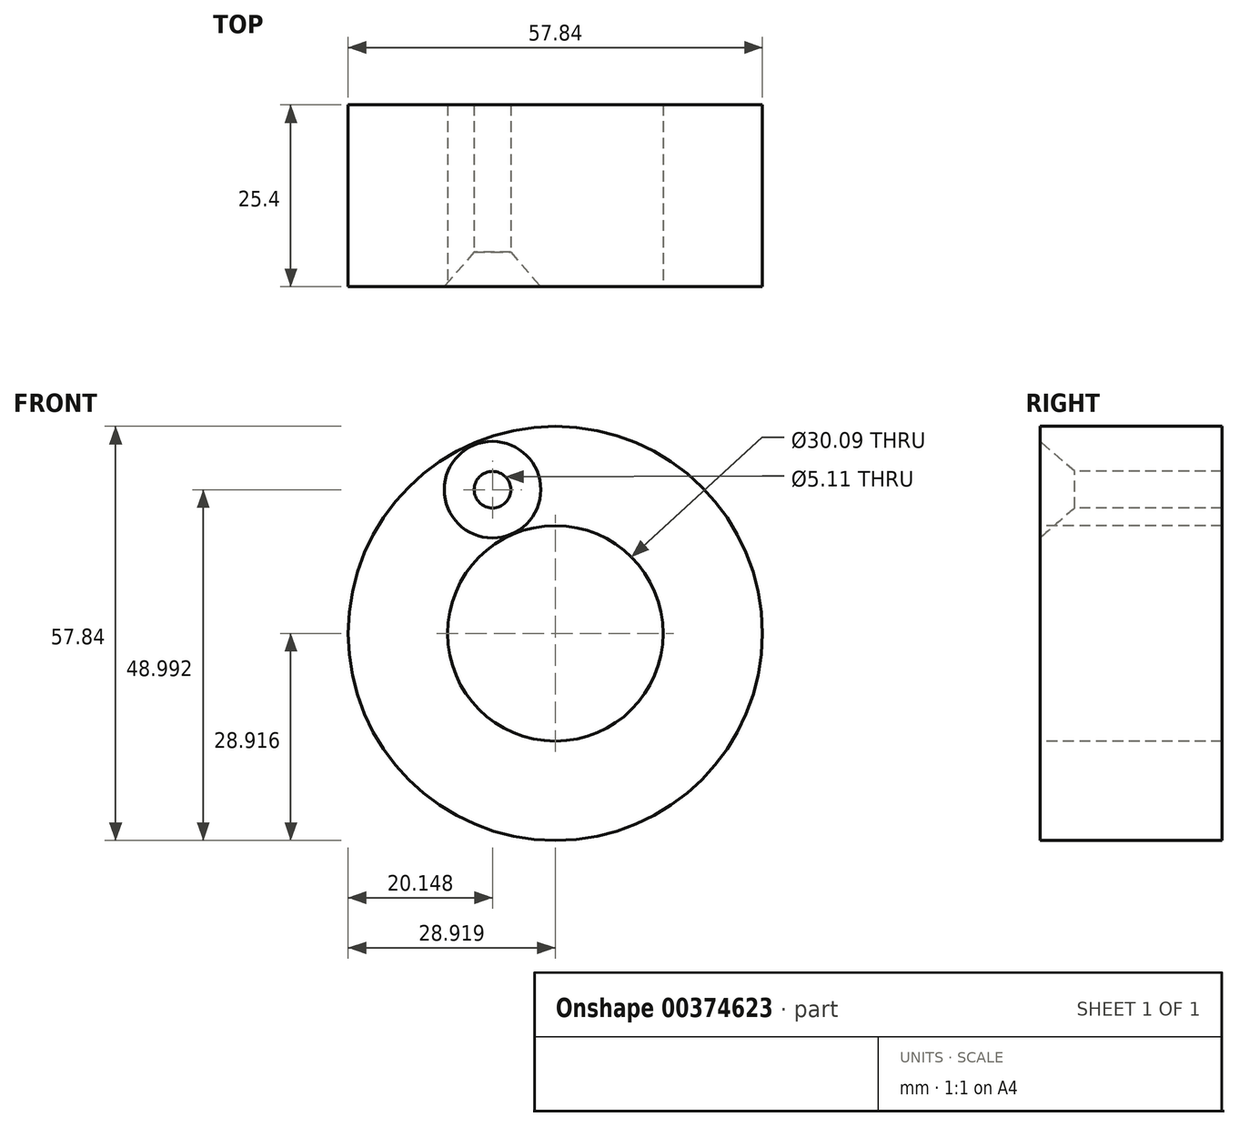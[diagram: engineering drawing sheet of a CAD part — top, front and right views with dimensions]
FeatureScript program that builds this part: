
annotation { "Feature Type Name" : "Feature", "Feature Type Description" : "" }
export const myFeature = defineFeature(function(context is Context, id is Id, definition is map)
    precondition{}
    {
        {
            var Q0;
            Q0=qCreatedBy(makeId("Front.planeOp"),FACE);
            var sketch = newSketch(context, id + "F0", { "sketchPlane" : qUnion([Q0])});
            skCircle(sketch, "E0", {"center": v(24.16, 38.02) * mm, "radius": 28.92 * mm});
            skSolve(sketch);
        }
        {
            var Q0;
            Q0=makeQuery(id+"F0.imprint","IMPRINT",FACE,{"disambiguationData":[TD([[makeQuery(id+"F0.imprint","IMPRINT",EDGE,{"derivedFrom":sQuery(id+"F0.wireOp",EDGE,"E0")}),1.0]])]});
            extrude(context, id + "F1", {"entities" : qUnion([Q0]), "depth" : 25.4 * mm});
        }
        {
            var Q0;
            Q0=makeQuery(id+"F1.opExtrude","CAP_FACE",FACE,{"disambiguationData":[OSD([sQuery(id+"F0.wireOp",EDGE,"E0")])],"isStart":false});
            var sketch = newSketch(context, id + "F2", { "sketchPlane" : qUnion([Q0])});
            skCircle(sketch, "E1", {"center": v(24.16, 38.02) * mm, "radius": 15.04 * mm});
            skSolve(sketch);
        }
        {
            var Q0;
            Q0=makeQuery(id+"F2.imprint","IMPRINT",FACE,{"disambiguationData":[TD([[makeQuery(id+"F2.imprint","IMPRINT",EDGE,{"derivedFrom":sQuery(id+"F2.wireOp",EDGE,"E1")}),1.0]])]});
            extrude(context, id + "F3", {"entities" : qUnion([Q0]), "operationType" : NewBodyOperationType.REMOVE, "endBound" : BoundingType.THROUGH_ALL, "oppositeDirection" : true, "depth" : 25.4 * mm});
        }
        {
            var Q0;
            Q0=makeQuery(id+"F1.opExtrude","CAP_FACE",FACE,{"disambiguationData":[OSD([sQuery(id+"F0.wireOp",EDGE,"E0")])],"isStart":false});
            var sketch = newSketch(context, id + "F4", { "sketchPlane" : qUnion([Q0])});
            skPoint(sketch, "E2", {"position": v(15.39, 58.1) * mm});
            skSolve(sketch);
        }
        {
            var Q0;
            Q0=sQuery(id+"F4.wireOp",VERTEX,"E2");
            var Q1;
            Q1=makeQuery(id+"F1.opExtrude","SWEPT_BODY",BODY,{"disambiguationData":[OSD([sQuery(id+"F0.wireOp",EDGE,"E0")])]});
            hole(context, id + "F5", {"style" : HoleStyle.C_SINK, "endStyle" : HoleEndStyle.THROUGH, "standardTappedOrClearance" : lookupTablePath({ "standard" : "ANSI", "engagement" : "75%", "pitch" : "20 tpi", "size" : "1/4", "type" : "Tapped" }), "standardBlindInLast" : lookupTablePath({ "standard" : "ANSI", "engagement" : "75%", "pitch" : "20 tpi", "size" : "1/4", "type" : "Tapped" }), "holeDiameter" : 5.1 * mm, "cSinkDiameter" : 13.5 * mm, "cSinkAngle" : 82 * degree, "showTappedDepth" : true, "isTappedThrough" : true, "tappedDepth" : 12.7 * mm, "tapClearance" : 3, "locations" : qUnion([Q0]), "scope" : qUnion([Q1]), "majorDiameter" : 6.35 * mm});
        }
    });
